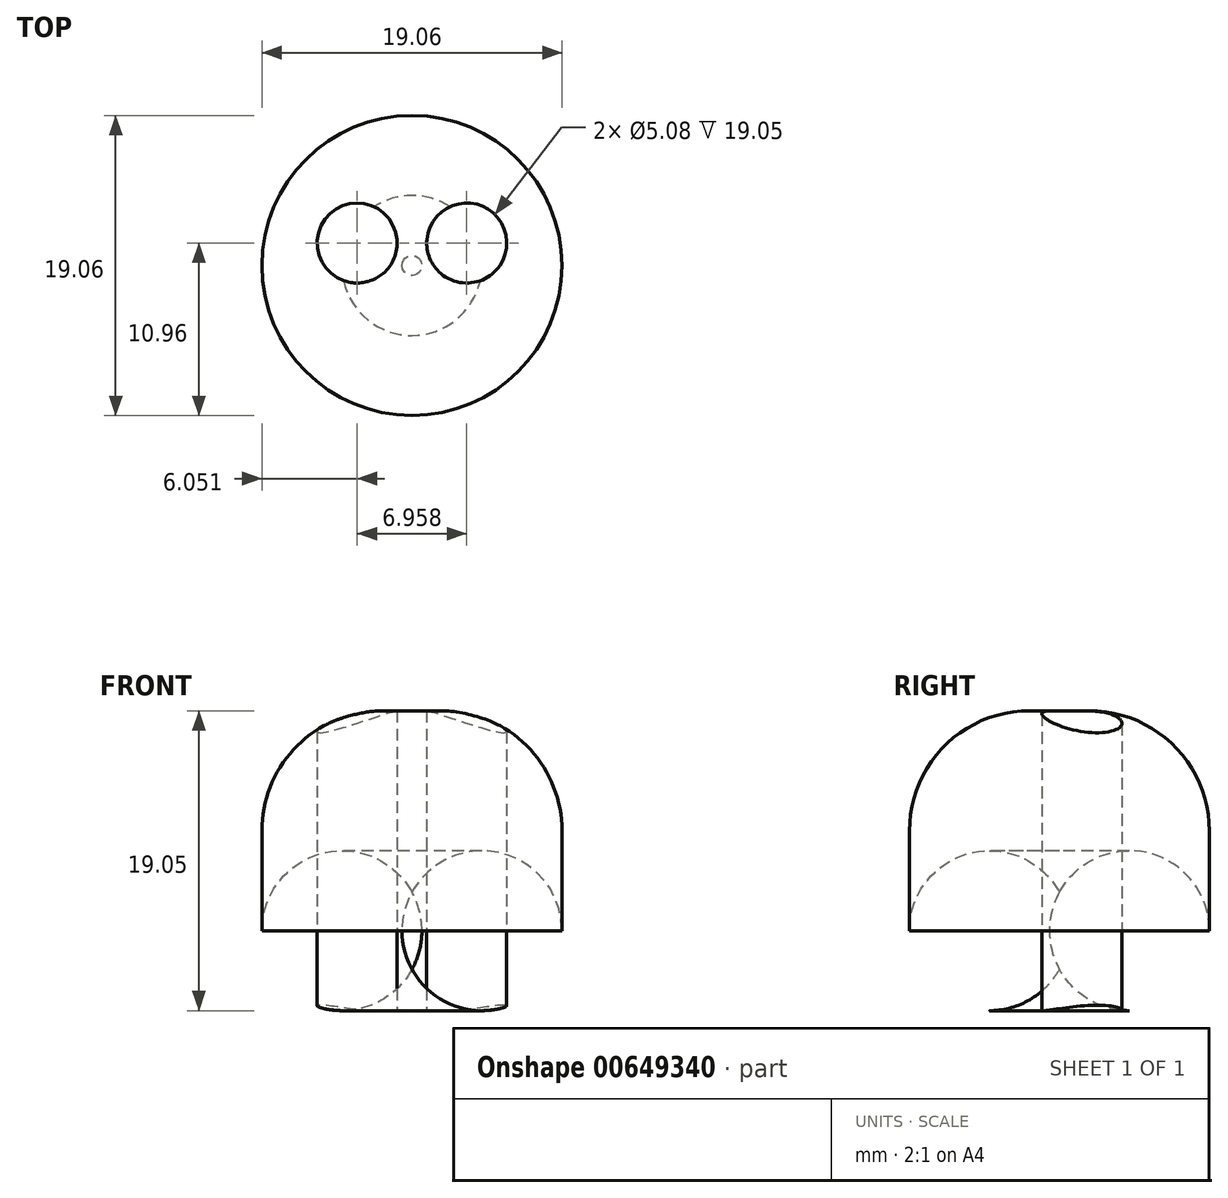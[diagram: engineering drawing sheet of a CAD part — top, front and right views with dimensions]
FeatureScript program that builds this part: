
annotation { "Feature Type Name" : "Feature", "Feature Type Description" : "" }
export const myFeature = defineFeature(function(context is Context, id is Id, definition is map)
    precondition{}
    {
        {
            var Q0;
            Q0=qCreatedBy(makeId("Top.planeOp"),FACE);
            var sketch = newSketch(context, id + "F0", { "sketchPlane" : qUnion([Q0])});
            skCircle(sketch, "E0", {"center": v(0, 0) * mm, "radius": 19.05 * mm});
            skCircle(sketch, "E1", {"center": v(0, 25.4) * mm, "radius": 9.53 * mm});
            skSolve(sketch);
        }
        {
            var Q0;
            {var subQ0=sQuery(id+"F0.wireOp",EDGE,"E1");var subQ1=sQuery(id+"F0.wireOp",EDGE,"E0");var subQ2=makeQuery(id+"F0.imprint","INTERSECT",VERTEX,{"disambiguationData":[OD(0.0)],"derivedFrom":[subQ1,subQ0]});Q0=makeQuery(id+"F0.imprint","IMPRINT",FACE,{"disambiguationData":[TD([[makeQuery(id+"F0.imprint","IMPRINT",EDGE,{"disambiguationData":[TD([[subQ2,-1.0]])],"derivedFrom":subQ1}),1.0]])]});}
            var Q1;
            {var subQ0=sQuery(id+"F0.wireOp",EDGE,"E1");var subQ1=sQuery(id+"F0.wireOp",EDGE,"E0");var subQ2=makeQuery(id+"F0.imprint","INTERSECT",VERTEX,{"disambiguationData":[OD(0.0)],"derivedFrom":[subQ1,subQ0]});Q1=makeQuery(id+"F0.imprint","IMPRINT",FACE,{"disambiguationData":[TD([[makeQuery(id+"F0.imprint","IMPRINT",EDGE,{"disambiguationData":[TD([[subQ2,1.0]])],"derivedFrom":subQ1}),1.0]])]});}
            extrude(context, id + "F1", {"entities" : qUnion([Q0, Q1]), "depth" : 25.4 * mm, "offsetDistance" : 25.4 * mm});
        }
        {
            var Q0;
            Q0=makeQuery(id+"F1.opExtrude","CAP_EDGE",EDGE,{"disambiguationData":[OSD([sQuery(id+"F0.wireOp",EDGE,"E0")])],"isStart":false});
            fillet(context, id + "F2", {"entities" : qUnion([Q0]), "radius" : 19.05 * mm, "tangentPropagation" : true, "allowEdgeOverflow" : false});
        }
        {
            var Q0;
            {var subQ0=sQuery(id+"F0.wireOp",EDGE,"E1");var subQ1=sQuery(id+"F0.wireOp",EDGE,"E0");var subQ2=makeQuery(id+"F0.imprint","INTERSECT",VERTEX,{"disambiguationData":[OD(0.0)],"derivedFrom":[subQ1,subQ0]});Q0=makeQuery(id+"F0.imprint","IMPRINT",FACE,{"disambiguationData":[TD([[makeQuery(id+"F0.imprint","IMPRINT",EDGE,{"disambiguationData":[TD([[subQ2,1.0]])],"derivedFrom":subQ1}),-1.0]])]});}
            var Q1;
            {var subQ0=sQuery(id+"F0.wireOp",EDGE,"E1");var subQ1=sQuery(id+"F0.wireOp",EDGE,"E0");var subQ2=makeQuery(id+"F0.imprint","INTERSECT",VERTEX,{"disambiguationData":[OD(0.0)],"derivedFrom":[subQ1,subQ0]});Q1=makeQuery(id+"F0.imprint","IMPRINT",FACE,{"disambiguationData":[TD([[makeQuery(id+"F0.imprint","IMPRINT",EDGE,{"disambiguationData":[TD([[subQ2,1.0]])],"derivedFrom":subQ1}),1.0]])]});}
            var Q2;
            Q2=sQuery(id+"F0.wireOp",EDGE,"E1");
            extrude(context, id + "F3", {"entities" : qUnion([Q0, Q1]), "surfaceEntities" : qUnion([Q2]), "depth" : 19.05 * mm, "offsetDistance" : 25.4 * mm});
        }
        {
            var Q0;
            Q0=makeQuery(id+"F3.opExtrude","CAP_EDGE",EDGE,{"disambiguationData":[OSD([sQuery(id+"F0.wireOp",EDGE,"E1")])],"isStart":false});
            fillet(context, id + "F4", {"entities" : qUnion([Q0]), "radius" : 7.62 * mm, "tangentPropagation" : true, "allowEdgeOverflow" : false});
        }
        {
            var Q0;
            Q0=makeQuery(id+"F3.opExtrude","CAP_EDGE",EDGE,{"disambiguationData":[OSD([sQuery(id+"F0.wireOp",EDGE,"E1")])],"isStart":true});
            fillet(context, id + "F5", {"entities" : qUnion([Q0]), "radius" : 5.08 * mm, "tangentPropagation" : true, "allowEdgeOverflow" : false});
        }
        {
            var Q0;
            Q0=qCreatedBy(makeId("Top.planeOp"),FACE);
            var sketch = newSketch(context, id + "F6", { "sketchPlane" : qUnion([Q0])});
            skLineSegment(sketch, "E2", {"start": v(-17.06, 9.5) * mm, "end": v(-26.59, 19.83) * mm});
            skLineSegment(sketch, "E3", {"start": v(-19.13, 0) * mm, "end": v(-33.25, 0) * mm});
            skLineSegment(sketch, "E4", {"start": v(-26.59, 19.83) * mm, "end": v(-23.9, 22.3) * mm});
            skLineSegment(sketch, "E5", {"start": v(-23.9, 22.3) * mm, "end": v(-14.8, 12.43) * mm});
            skLineSegment(sketch, "E6", {"start": v(-33.25, 0) * mm, "end": v(-33.25, 3.67) * mm});
            skLineSegment(sketch, "E7", {"start": v(-33.25, 3.67) * mm, "end": v(-18.83, 3.67) * mm});
            skLineSegment(sketch, "E8", {"start": v(-14.8, 12.43) * mm, "end": v(-12.99, 10.47) * mm});
            skLineSegment(sketch, "E9", {"start": v(-12.99, 10.47) * mm, "end": v(-13.9, 5.77) * mm});
            skPoint(sketch, "E9.endSnap0", {"position": v(-13.9, 11.45) * mm});
            skLineSegment(sketch, "E10", {"start": v(-13.9, 5.77) * mm, "end": v(-17.06, 9.5) * mm});
            skLineSegment(sketch, "E11", {"start": v(-18.83, 3.67) * mm, "end": v(-13.48, 3.67) * mm});
            skLineSegment(sketch, "E12", {"start": v(-13.48, 3.67) * mm, "end": v(-13.48, 0) * mm});
            skLineSegment(sketch, "E13", {"start": v(-13.48, 0) * mm, "end": v(-19.13, 0) * mm});
            skLineSegment(sketch, "E14.MirrorCS", {"start": v(-14.8, -12.43) * mm, "end": v(-12.99, -10.47) * mm});
            skLineSegment(sketch, "E15.MirrorCS", {"start": v(-12.99, -10.47) * mm, "end": v(-13.9, -5.77) * mm});
            skLineSegment(sketch, "E16.MirrorCS", {"start": v(-13.9, -5.77) * mm, "end": v(-17.06, -9.5) * mm});
            skLineSegment(sketch, "E17.MirrorCS", {"start": v(-23.9, -22.3) * mm, "end": v(-14.8, -12.43) * mm});
            skLineSegment(sketch, "E18.MirrorCS", {"start": v(-17.06, -9.5) * mm, "end": v(-26.59, -19.83) * mm});
            skLineSegment(sketch, "E19.MirrorCS", {"start": v(-26.59, -19.83) * mm, "end": v(-23.9, -22.3) * mm});
            skPoint(sketch, "E20.MirrorP", {"position": v(-13.9, -11.45) * mm});
            skLineSegment(sketch, "E21.MirrorCS", {"start": v(14.8, -12.43) * mm, "end": v(12.99, -10.47) * mm});
            skLineSegment(sketch, "E22.MirrorCS", {"start": v(14.8, 12.43) * mm, "end": v(12.99, 10.47) * mm});
            skPoint(sketch, "E23.MirrorP", {"position": v(13.9, 11.45) * mm});
            skLineSegment(sketch, "E24.MirrorCS", {"start": v(26.59, -19.83) * mm, "end": v(23.9, -22.3) * mm});
            skLineSegment(sketch, "E25.MirrorCS", {"start": v(13.48, 0) * mm, "end": v(19.13, 0) * mm});
            skLineSegment(sketch, "E26.MirrorCS", {"start": v(13.48, 3.67) * mm, "end": v(13.48, 0) * mm});
            skLineSegment(sketch, "E27.MirrorCS", {"start": v(18.83, 3.67) * mm, "end": v(13.48, 3.67) * mm});
            skLineSegment(sketch, "E28.MirrorCS", {"start": v(23.9, -22.3) * mm, "end": v(14.8, -12.43) * mm});
            skLineSegment(sketch, "E29.MirrorCS", {"start": v(17.06, 9.5) * mm, "end": v(26.59, 19.83) * mm});
            skLineSegment(sketch, "E30.MirrorCS", {"start": v(19.13, 0) * mm, "end": v(33.25, 0) * mm});
            skLineSegment(sketch, "E31.MirrorCS", {"start": v(26.59, 19.83) * mm, "end": v(23.9, 22.3) * mm});
            skLineSegment(sketch, "E32.MirrorCS", {"start": v(13.9, -5.77) * mm, "end": v(17.06, -9.5) * mm});
            skPoint(sketch, "E33.MirrorP", {"position": v(13.9, -11.45) * mm});
            skLineSegment(sketch, "E34.MirrorCS", {"start": v(23.9, 22.3) * mm, "end": v(14.8, 12.43) * mm});
            skLineSegment(sketch, "E35.MirrorCS", {"start": v(33.25, 0) * mm, "end": v(33.25, 3.67) * mm});
            skLineSegment(sketch, "E36.MirrorCS", {"start": v(12.99, -10.47) * mm, "end": v(13.9, -5.77) * mm});
            skLineSegment(sketch, "E37.MirrorCS", {"start": v(12.99, 10.47) * mm, "end": v(13.9, 5.77) * mm});
            skLineSegment(sketch, "E38.MirrorCS", {"start": v(33.25, 3.67) * mm, "end": v(18.83, 3.67) * mm});
            skLineSegment(sketch, "E39.MirrorCS", {"start": v(13.9, 5.77) * mm, "end": v(17.06, 9.5) * mm});
            skLineSegment(sketch, "E40.MirrorCS", {"start": v(17.06, -9.5) * mm, "end": v(26.59, -19.83) * mm});
            skSolve(sketch);
        }
        {
            var Q0;
            Q0 = qSketchRegion(id + "F6", true);
            extrude(context, id + "F7", {"entities" : qUnion([Q0]), "operationType" : NewBodyOperationType.ADD, "depth" : 6.35 * mm, "offsetDistance" : 25.4 * mm});
        }
        {
            var Q0;
            Q0=qCreatedBy(makeId("Top.planeOp"),FACE);
            var sketch = newSketch(context, id + "F8", { "sketchPlane" : qUnion([Q0])});
            skText(sketch, "E41", { "text": "cooper", "fontName": "OpenSans-Bold.ttf"});
            const initialGuessF8  = {"E41": [-0.01428, -0.00285, 1, 0, 0.00635]};
            skSetInitialGuess(sketch, initialGuessF8);
            skSolve(sketch);
        }
        {
            var Q0;
            Q0 = qSketchRegion(id + "F8", true);
            extrude(context, id + "F9", {"entities" : qUnion([Q0]), "operationType" : NewBodyOperationType.REMOVE, "endBound" : BoundingType.THROUGH_ALL, "depth" : 25.4 * mm, "offsetDistance" : 25.4 * mm});
        }
        {
            var Q0;
            Q0=qCreatedBy(makeId("Top.planeOp"),FACE);
            var sketch = newSketch(context, id + "F10", { "sketchPlane" : qUnion([Q0])});
            skCircle(sketch, "E42", {"center": v(-3.48, 26.83) * mm, "radius": 2.54 * mm});
            skCircle(sketch, "E43.MirrorC", {"center": v(3.48, 26.83) * mm, "radius": 2.54 * mm});
            skSolve(sketch);
        }
        {
            var Q0;
            Q0 = qSketchRegion(id + "F10", true);
            extrude(context, id + "F11", {"entities" : qUnion([Q0]), "operationType" : NewBodyOperationType.REMOVE, "endBound" : BoundingType.THROUGH_ALL, "depth" : 25.4 * mm, "offsetDistance" : 25.4 * mm});
        }
        {
            var Q0;
            Q0=makeQuery(id+"F9.boolean.opBoolean","SPLIT",BODY,{"disambiguationData":[OD(4.0)],"derivedFrom":makeQuery(id+"F1.opExtrude","SWEPT_BODY",BODY,{"disambiguationData":[OSD([sQuery(id+"F0.wireOp",EDGE,"E0")])]})});
            var Q1;
            Q1=makeQuery(id+"F9.boolean.opBoolean","SPLIT",BODY,{"disambiguationData":[OD(3.0)],"derivedFrom":makeQuery(id+"F1.opExtrude","SWEPT_BODY",BODY,{"disambiguationData":[OSD([sQuery(id+"F0.wireOp",EDGE,"E0")])]})});
            var Q2;
            Q2=makeQuery(id+"F9.boolean.opBoolean","SPLIT",BODY,{"disambiguationData":[OD(2.0)],"derivedFrom":makeQuery(id+"F1.opExtrude","SWEPT_BODY",BODY,{"disambiguationData":[OSD([sQuery(id+"F0.wireOp",EDGE,"E0")])]})});
            var Q3;
            Q3=makeQuery(id+"F9.boolean.opBoolean","SPLIT",BODY,{"disambiguationData":[OD(1.0)],"derivedFrom":makeQuery(id+"F1.opExtrude","SWEPT_BODY",BODY,{"disambiguationData":[OSD([sQuery(id+"F0.wireOp",EDGE,"E0")])]})});
            deleteBodies(context, id + "F12", {"entities" : qUnion([Q0, Q1, Q2, Q3])});
        }
    });
